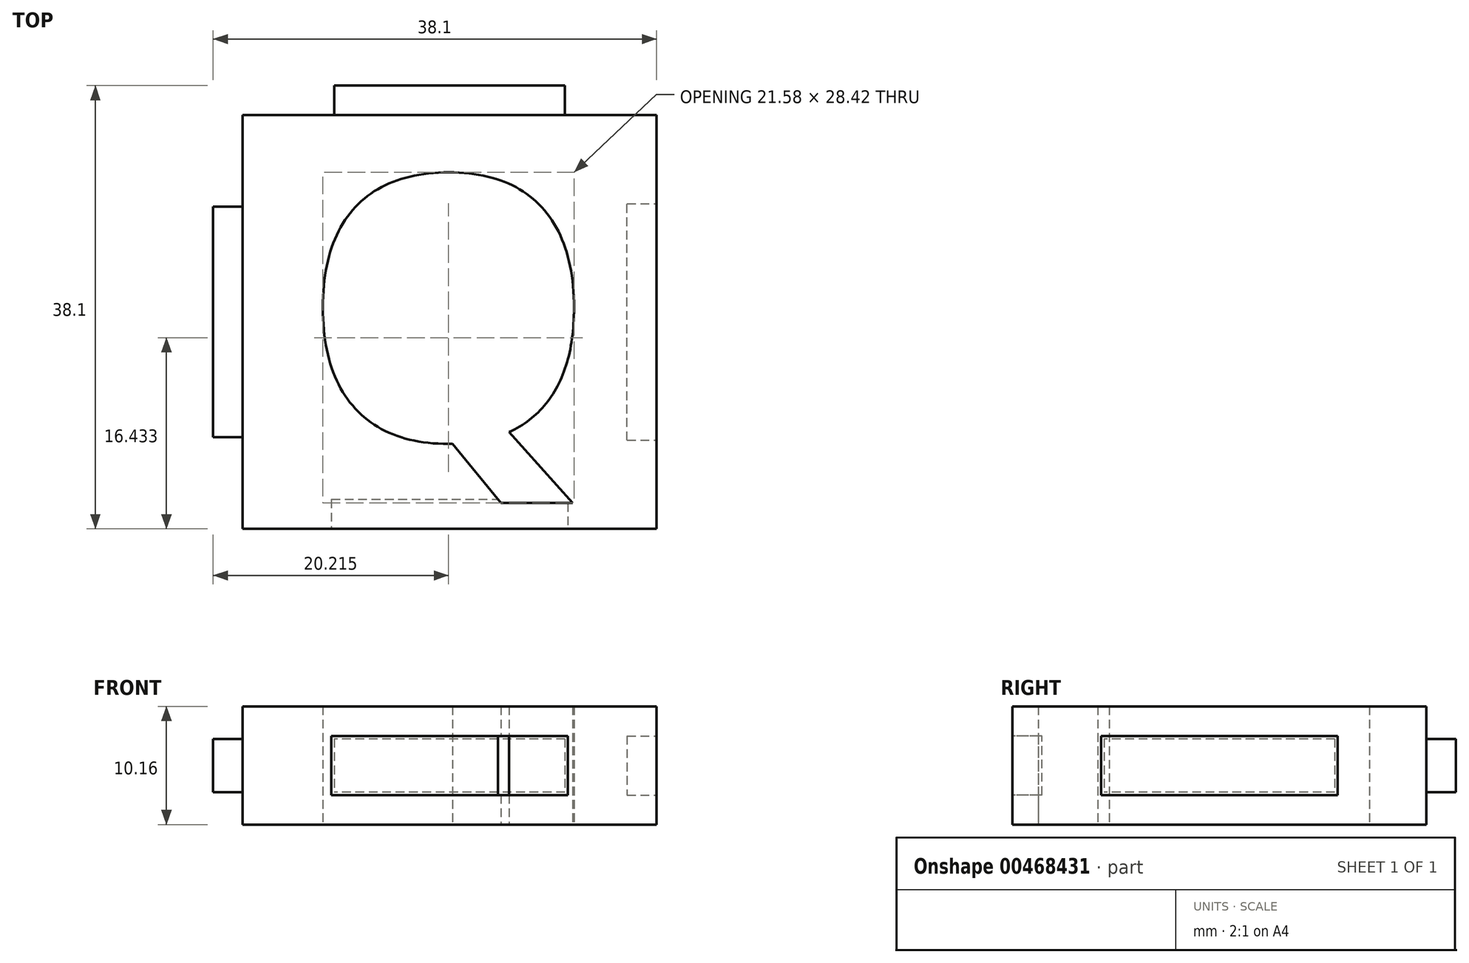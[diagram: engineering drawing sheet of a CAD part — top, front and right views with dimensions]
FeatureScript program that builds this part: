
annotation { "Feature Type Name" : "Feature", "Feature Type Description" : "" }
export const myFeature = defineFeature(function(context is Context, id is Id, definition is map)
    precondition{}
    {
        {
            var Q0;
            Q0=qCreatedBy(makeId("Top.planeOp"),FACE);
            var sketch = newSketch(context, id + "F0", { "sketchPlane" : qUnion([Q0])});
            skLineSegment(sketch, "E0.bottom", {"start": v(-17.78, 17.78) * mm, "end": v(17.78, 17.78) * mm});
            skLineSegment(sketch, "E0.top", {"start": v(-17.78, -17.78) * mm, "end": v(17.78, -17.78) * mm});
            skLineSegment(sketch, "E0.left", {"start": v(-17.78, 17.78) * mm, "end": v(-17.78, -17.78) * mm});
            skLineSegment(sketch, "E0.right", {"start": v(17.78, 17.78) * mm, "end": v(17.78, -17.78) * mm});
            skText(sketch, "E1", { "text": "Q", "fontName": "OpenSans-Bold.ttf"});
            const initialGuessF0  = {"E1": [-0.01274, -0.01016, 1, 0, 0.02286]};
            skSetInitialGuess(sketch, initialGuessF0);
            skSolve(sketch);
        }
        {
            var Q0;
            Q0=qSketchRegion(id+"F0",true);
            extrude(context, id + "F1", {"entities" : qUnion([Q0]), "endBound" : BoundingType.SYMMETRIC, "depth" : 10.16 * mm});
        }
        {
            var Q0;
            Q0=makeQuery(id+"F1.opExtrude","SWEPT_FACE",FACE,{"disambiguationData":[OSD([sQuery(id+"F0.wireOp",EDGE,"E0.bottom")])]});
            var sketch = newSketch(context, id + "F2", { "sketchPlane" : qUnion([Q0])});
            skLineSegment(sketch, "E2.bottom", {"start": v(-9.9, 2.29) * mm, "end": v(9.9, 2.29) * mm});
            skLineSegment(sketch, "E2.top", {"start": v(-9.9, -2.29) * mm, "end": v(9.9, -2.29) * mm});
            skLineSegment(sketch, "E2.left", {"start": v(-9.9, 2.29) * mm, "end": v(-9.9, -2.29) * mm});
            skLineSegment(sketch, "E2.right", {"start": v(9.9, 2.29) * mm, "end": v(9.9, -2.29) * mm});
            skSolve(sketch);
        }
        {
            var Q0;
            Q0=qSketchRegion(id+"F2",true);
            extrude(context, id + "F3", {"entities" : qUnion([Q0]), "operationType" : NewBodyOperationType.ADD, "depth" : 2.54 * mm});
        }
        {
            var Q0;
            Q0=makeQuery(id+"F1.opExtrude","SWEPT_FACE",FACE,{"disambiguationData":[OSD([sQuery(id+"F0.wireOp",EDGE,"E0.left")])]});
            var sketch = newSketch(context, id + "F4", { "sketchPlane" : qUnion([Q0])});
            skLineSegment(sketch, "E3.bottom", {"start": v(-9.9, 2.29) * mm, "end": v(9.9, 2.29) * mm});
            skLineSegment(sketch, "E3.top", {"start": v(-9.9, -2.29) * mm, "end": v(9.9, -2.29) * mm});
            skLineSegment(sketch, "E3.left", {"start": v(-9.9, 2.29) * mm, "end": v(-9.9, -2.29) * mm});
            skLineSegment(sketch, "E3.right", {"start": v(9.9, 2.29) * mm, "end": v(9.9, -2.29) * mm});
            skSolve(sketch);
        }
        {
            var Q0;
            Q0=qSketchRegion(id+"F4",true);
            extrude(context, id + "F5", {"entities" : qUnion([Q0]), "operationType" : NewBodyOperationType.ADD, "depth" : 2.54 * mm});
        }
        {
            var Q0;
            Q0=makeQuery(id+"F1.opExtrude","SWEPT_FACE",FACE,{"disambiguationData":[OSD([sQuery(id+"F0.wireOp",EDGE,"E0.top")])]});
            var sketch = newSketch(context, id + "F6", { "sketchPlane" : qUnion([Q0])});
            skLineSegment(sketch, "E4.bottom", {"start": v(-10.16, 2.54) * mm, "end": v(10.16, 2.54) * mm});
            skLineSegment(sketch, "E4.top", {"start": v(-10.16, -2.54) * mm, "end": v(10.16, -2.54) * mm});
            skLineSegment(sketch, "E4.left", {"start": v(-10.16, 2.54) * mm, "end": v(-10.16, -2.54) * mm});
            skLineSegment(sketch, "E4.right", {"start": v(10.16, 2.54) * mm, "end": v(10.16, -2.54) * mm});
            skSolve(sketch);
        }
        {
            var Q0;
            Q0=qSketchRegion(id+"F6",true);
            extrude(context, id + "F7", {"entities" : qUnion([Q0]), "operationType" : NewBodyOperationType.REMOVE, "oppositeDirection" : true, "depth" : 2.54 * mm});
        }
        {
            var Q0;
            Q0=makeQuery(id+"F1.opExtrude","SWEPT_FACE",FACE,{"disambiguationData":[OSD([sQuery(id+"F0.wireOp",EDGE,"E0.right")])]});
            var sketch = newSketch(context, id + "F8", { "sketchPlane" : qUnion([Q0])});
            skLineSegment(sketch, "E5.bottom", {"start": v(-10.16, 2.54) * mm, "end": v(10.16, 2.54) * mm});
            skLineSegment(sketch, "E5.top", {"start": v(-10.16, -2.54) * mm, "end": v(10.16, -2.54) * mm});
            skLineSegment(sketch, "E5.left", {"start": v(-10.16, 2.54) * mm, "end": v(-10.16, -2.54) * mm});
            skLineSegment(sketch, "E5.right", {"start": v(10.16, 2.54) * mm, "end": v(10.16, -2.54) * mm});
            skSolve(sketch);
        }
        {
            var Q0;
            Q0=qSketchRegion(id+"F8",true);
            extrude(context, id + "F9", {"entities" : qUnion([Q0]), "operationType" : NewBodyOperationType.REMOVE, "oppositeDirection" : true, "depth" : 2.54 * mm});
        }
    });
